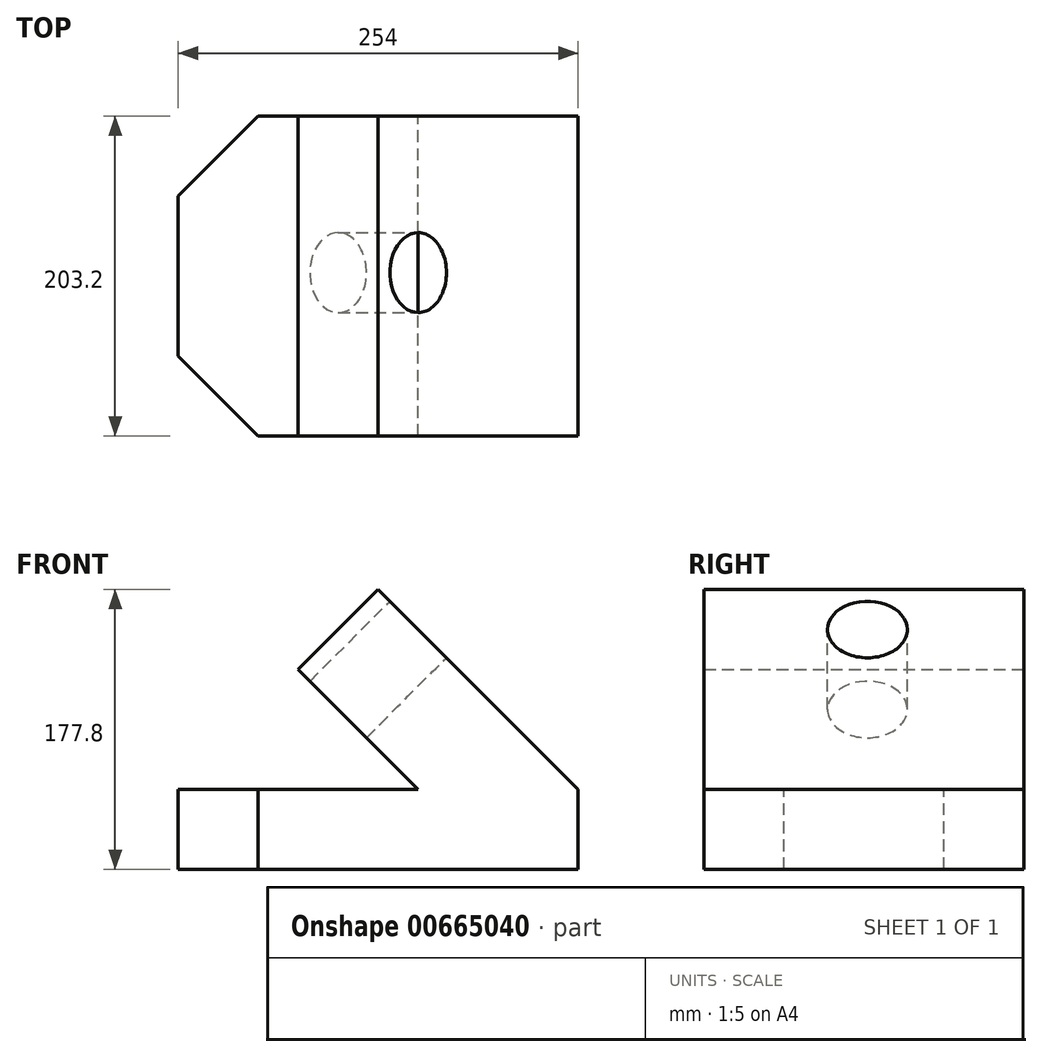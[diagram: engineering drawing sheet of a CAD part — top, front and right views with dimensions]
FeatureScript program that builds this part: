
annotation { "Feature Type Name" : "Feature", "Feature Type Description" : "" }
export const myFeature = defineFeature(function(context is Context, id is Id, definition is map)
    precondition{}
    {
        {
            var Q0;
            Q0=qCreatedBy(makeId("Front.planeOp"),FACE);
            var sketch = newSketch(context, id + "F0", { "sketchPlane" : qUnion([Q0])});
            skLineSegment(sketch, "E0", {"start": v(0, 0) * mm, "end": v(0, 50.8) * mm});
            skLineSegment(sketch, "E1", {"start": v(0, 50.8) * mm, "end": v(152.4, 50.8) * mm});
            skLineSegment(sketch, "E2", {"start": v(0, 0) * mm, "end": v(254, 0) * mm});
            skLineSegment(sketch, "E3", {"start": v(254, 0) * mm, "end": v(254, 50.8) * mm});
            skLineSegment(sketch, "E4", {"start": v(76.2, 127) * mm, "end": v(152.4, 50.8) * mm});
            skLineSegment(sketch, "E5", {"start": v(127, 177.8) * mm, "end": v(254, 50.8) * mm});
            skLineSegment(sketch, "E6", {"start": v(76.2, 127) * mm, "end": v(127, 177.8) * mm});
            skSolve(sketch);
        }
        {
            var Q0;
            Q0=makeQuery(id+"F0.imprint","IMPRINT",FACE,{"disambiguationData":[TD([[makeQuery(id+"F0.imprint","IMPRINT",EDGE,{"derivedFrom":sQuery(id+"F0.wireOp",EDGE,"E0")}),-1.0]])]});
            extrude(context, id + "F1", {"entities" : qUnion([Q0]), "endBound" : BoundingType.SYMMETRIC, "depth" : 203.2 * mm, "offsetDistance" : 25.4 * mm});
        }
        {
            var Q0;
            Q0=makeQuery(id+"F1.opExtrude","SWEPT_FACE",FACE,{"disambiguationData":[OSD([sQuery(id+"F0.wireOp",EDGE,"E1")])]});
            var sketch = newSketch(context, id + "F2", { "sketchPlane" : qUnion([Q0])});
            skLineSegment(sketch, "E7", {"start": v(0, 0) * mm, "end": v(0, 50.8) * mm});
            skLineSegment(sketch, "E8", {"start": v(0, 50.8) * mm, "end": v(0, 101.6) * mm});
            skLineSegment(sketch, "E9", {"start": v(0, 0) * mm, "end": v(0, -50.8) * mm});
            skLineSegment(sketch, "E10", {"start": v(0, -50.8) * mm, "end": v(0, -101.6) * mm});
            skLineSegment(sketch, "E11", {"start": v(0, -101.6) * mm, "end": v(50.8, -101.6) * mm});
            skLineSegment(sketch, "E12", {"start": v(50.8, -101.6) * mm, "end": v(0, -50.8) * mm});
            skLineSegment(sketch, "E13", {"start": v(0, 101.6) * mm, "end": v(50.8, 101.6) * mm});
            skLineSegment(sketch, "E14", {"start": v(50.8, 101.6) * mm, "end": v(0, 50.8) * mm});
            skSolve(sketch);
        }
        {
            var Q0;
            Q0=makeQuery(id+"F2.imprint","IMPRINT",FACE,{"disambiguationData":[TD([[makeQuery(id+"F2.imprint","IMPRINT",EDGE,{"derivedFrom":sQuery(id+"F2.wireOp",EDGE,"E8")}),-1.0]])]});
            var Q1;
            Q1=makeQuery(id+"F2.imprint","IMPRINT",FACE,{"disambiguationData":[TD([[makeQuery(id+"F2.imprint","IMPRINT",EDGE,{"derivedFrom":sQuery(id+"F2.wireOp",EDGE,"E10")}),-1.0]])]});
            extrude(context, id + "F3", {"entities" : qUnion([Q0, Q1]), "operationType" : NewBodyOperationType.REMOVE, "oppositeDirection" : true, "depth" : 50.8 * mm, "offsetDistance" : 25.4 * mm});
        }
        {
            var Q0;
            Q0=makeQuery(id+"F1.opExtrude","SWEPT_FACE",FACE,{"disambiguationData":[OSD([sQuery(id+"F0.wireOp",EDGE,"E5")])]});
            var sketch = newSketch(context, id + "F4", { "sketchPlane" : qUnion([Q0])});
            skCircle(sketch, "E15", {"center": v(2.18, 0) * mm, "radius": 25.4 * mm});
            skSolve(sketch);
        }
        {
            var Q0;
            Q0=makeQuery(id+"F4.imprint","IMPRINT",FACE,{"disambiguationData":[TD([[makeQuery(id+"F4.imprint","IMPRINT",EDGE,{"derivedFrom":sQuery(id+"F4.wireOp",EDGE,"E15")}),1.0]])]});
            extrude(context, id + "F5", {"entities" : qUnion([Q0]), "operationType" : NewBodyOperationType.REMOVE, "oppositeDirection" : true, "depth" : 88.9 * mm, "offsetDistance" : 25.4 * mm});
        }
    });
